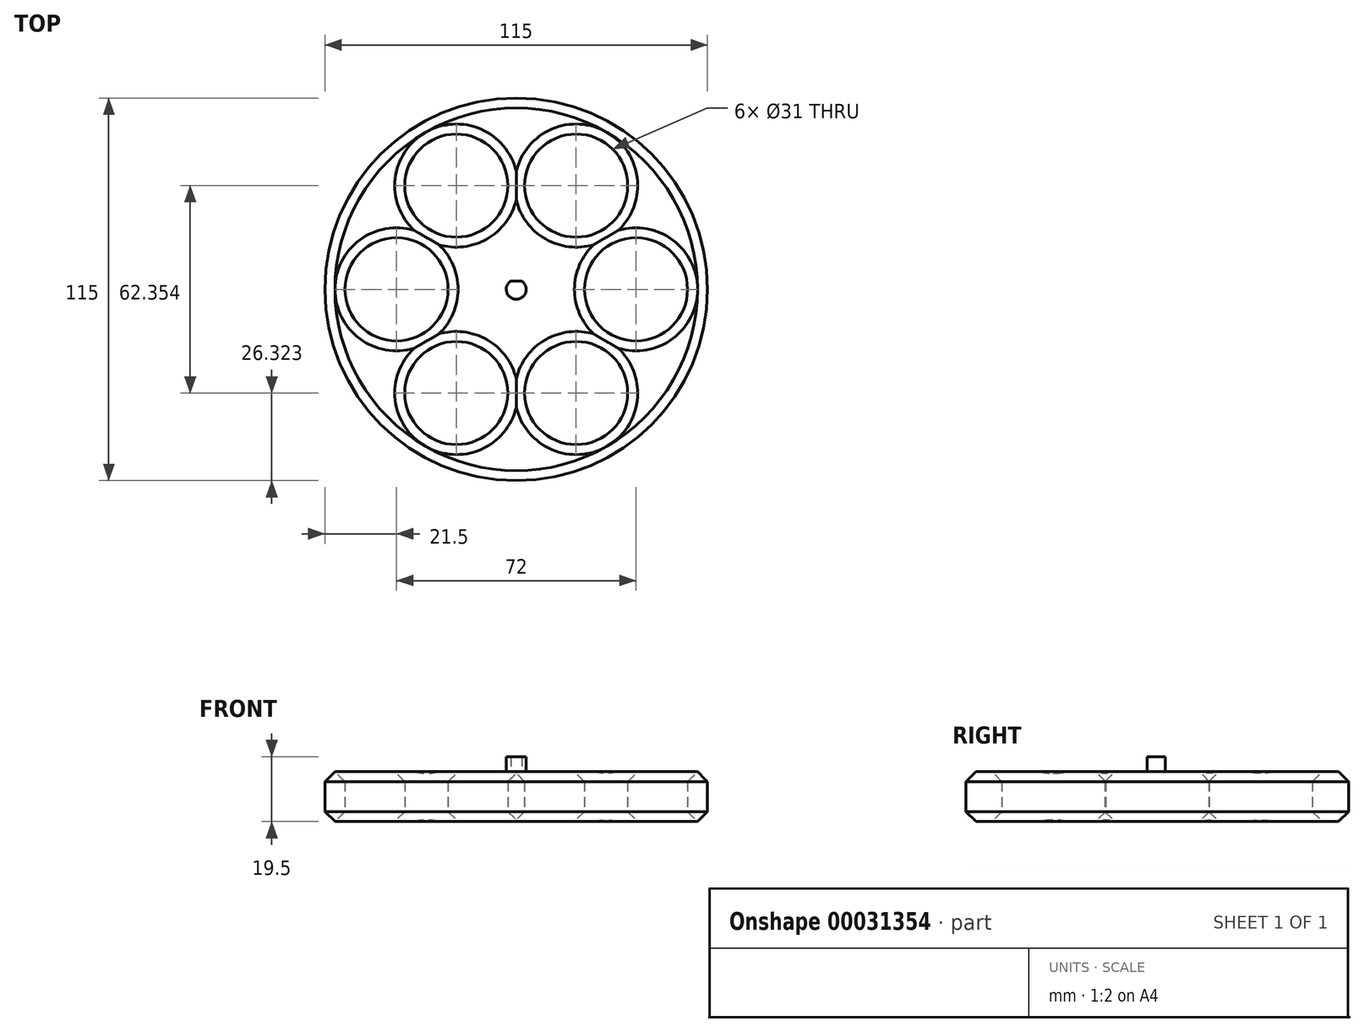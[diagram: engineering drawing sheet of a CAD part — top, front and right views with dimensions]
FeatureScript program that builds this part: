
annotation { "Feature Type Name" : "Feature", "Feature Type Description" : "" }
export const myFeature = defineFeature(function(context is Context, id is Id, definition is map)
    precondition{}
    {
        {
            var Q0;
            Q0=qCreatedBy(makeId("Top.planeOp"),FACE);
            var sketch = newSketch(context, id + "F0", { "sketchPlane" : qUnion([Q0])});
            skCircle(sketch, "E0", {"center": v(0, 0) * mm, "radius": 57.5 * mm});
            skCircle(sketch, "E1", {"center": v(-36, 0) * mm, "radius": 15.5 * mm});
            skCircle(sketch, "E2.1.0", {"center": v(-18, 31.18) * mm, "radius": 15.5 * mm});
            skCircle(sketch, "E2.2.0", {"center": v(18, 31.18) * mm, "radius": 15.5 * mm});
            skCircle(sketch, "E2.3.0", {"center": v(36, 0) * mm, "radius": 15.5 * mm});
            skCircle(sketch, "E2.4.0", {"center": v(18, -31.18) * mm, "radius": 15.5 * mm});
            skCircle(sketch, "E2.5.0", {"center": v(-18, -31.18) * mm, "radius": 15.5 * mm});
            skLineSegment(sketch, "E2.anchor1", {"start": v(0, 0) * mm, "end": v(-36, 0) * mm, "construction": true});
            skLineSegment(sketch, "E2.anchor2", {"start": v(0, 0) * mm, "end": v(-18, -31.18) * mm, "construction": true});
            skSolve(sketch);
        }
        {
            var Q0;
            Q0 = qSketchRegion(id + "F0", true);
            extrude(context, id + "F1", {"entities" : qUnion([Q0]), "depth" : 15 * mm});
        }
        {
            var Q0;
            Q0=makeQuery(id+"F1.opExtrude","CAP_FACE",FACE,{"disambiguationData":[OSD([sQuery(id+"F0.wireOp",EDGE,"E0"),sQuery(id+"F0.wireOp",EDGE,"E1"),sQuery(id+"F0.wireOp",EDGE,"E2.1.0"),sQuery(id+"F0.wireOp",EDGE,"E2.2.0"),sQuery(id+"F0.wireOp",EDGE,"E2.3.0"),sQuery(id+"F0.wireOp",EDGE,"E2.4.0"),sQuery(id+"F0.wireOp",EDGE,"E2.5.0")])],"isStart":false});
            var sketch = newSketch(context, id + "F2", { "sketchPlane" : qUnion([Q0])});
            skArc(sketch, "E3", {"start": v(-1.66, 2.5) * mm, "mid": v(0, -3) * mm, "end": v(1.66, 2.5) * mm});
            skLineSegment(sketch, "E4", {"start": v(-1.66, 2.5) * mm, "end": v(1.66, 2.5) * mm});
            skSolve(sketch);
        }
        {
            var Q0;
            Q0 = qSketchRegion(id + "F2", true);
            extrude(context, id + "F3", {"entities" : qUnion([Q0]), "operationType" : NewBodyOperationType.ADD, "depth" : 4.5 * mm});
        }
        {
            var Q0;
            Q0=makeQuery(id+"F1.opExtrude","CAP_EDGE",EDGE,{"disambiguationData":[OSD([sQuery(id+"F0.wireOp",EDGE,"E0")])],"isStart":false});
            var Q1;
            Q1=makeQuery(id+"F1.opExtrude","CAP_EDGE",EDGE,{"disambiguationData":[OSD([sQuery(id+"F0.wireOp",EDGE,"E0")])],"isStart":true});
            var Q2;
            Q2=makeQuery(id+"F1.opExtrude","CAP_EDGE",EDGE,{"disambiguationData":[OSD([sQuery(id+"F0.wireOp",EDGE,"E2.2.0")])],"isStart":false});
            var Q3;
            Q3=makeQuery(id+"F1.opExtrude","CAP_EDGE",EDGE,{"disambiguationData":[OSD([sQuery(id+"F0.wireOp",EDGE,"E2.3.0")])],"isStart":false});
            var Q4;
            Q4=makeQuery(id+"F1.opExtrude","CAP_EDGE",EDGE,{"disambiguationData":[OSD([sQuery(id+"F0.wireOp",EDGE,"E2.4.0")])],"isStart":false});
            var Q5;
            Q5=makeQuery(id+"F1.opExtrude","CAP_EDGE",EDGE,{"disambiguationData":[OSD([sQuery(id+"F0.wireOp",EDGE,"E2.5.0")])],"isStart":false});
            var Q6;
            Q6=makeQuery(id+"F1.opExtrude","CAP_EDGE",EDGE,{"disambiguationData":[OSD([sQuery(id+"F0.wireOp",EDGE,"E1")])],"isStart":false});
            var Q7;
            Q7=makeQuery(id+"F1.opExtrude","CAP_EDGE",EDGE,{"disambiguationData":[OSD([sQuery(id+"F0.wireOp",EDGE,"E2.1.0")])],"isStart":false});
            var Q8;
            Q8=makeQuery(id+"F1.opExtrude","CAP_EDGE",EDGE,{"disambiguationData":[OSD([sQuery(id+"F0.wireOp",EDGE,"E2.2.0")])],"isStart":true});
            var Q9;
            Q9=makeQuery(id+"F1.opExtrude","CAP_EDGE",EDGE,{"disambiguationData":[OSD([sQuery(id+"F0.wireOp",EDGE,"E2.3.0")])],"isStart":true});
            var Q10;
            Q10=makeQuery(id+"F1.opExtrude","CAP_EDGE",EDGE,{"disambiguationData":[OSD([sQuery(id+"F0.wireOp",EDGE,"E2.4.0")])],"isStart":true});
            var Q11;
            Q11=makeQuery(id+"F1.opExtrude","CAP_EDGE",EDGE,{"disambiguationData":[OSD([sQuery(id+"F0.wireOp",EDGE,"E2.5.0")])],"isStart":true});
            var Q12;
            Q12=makeQuery(id+"F1.opExtrude","CAP_EDGE",EDGE,{"disambiguationData":[OSD([sQuery(id+"F0.wireOp",EDGE,"E1")])],"isStart":true});
            var Q13;
            Q13=makeQuery(id+"F1.opExtrude","CAP_EDGE",EDGE,{"disambiguationData":[OSD([sQuery(id+"F0.wireOp",EDGE,"E2.1.0")])],"isStart":true});
            chamfer(context, id + "F4", {"entities" : qUnion([Q0, Q1, Q2, Q3, Q4, Q5, Q6, Q7, Q8, Q9, Q10, Q11, Q12, Q13]), "width" : 3 * mm, "tangentPropagation" : true});
        }
    });
